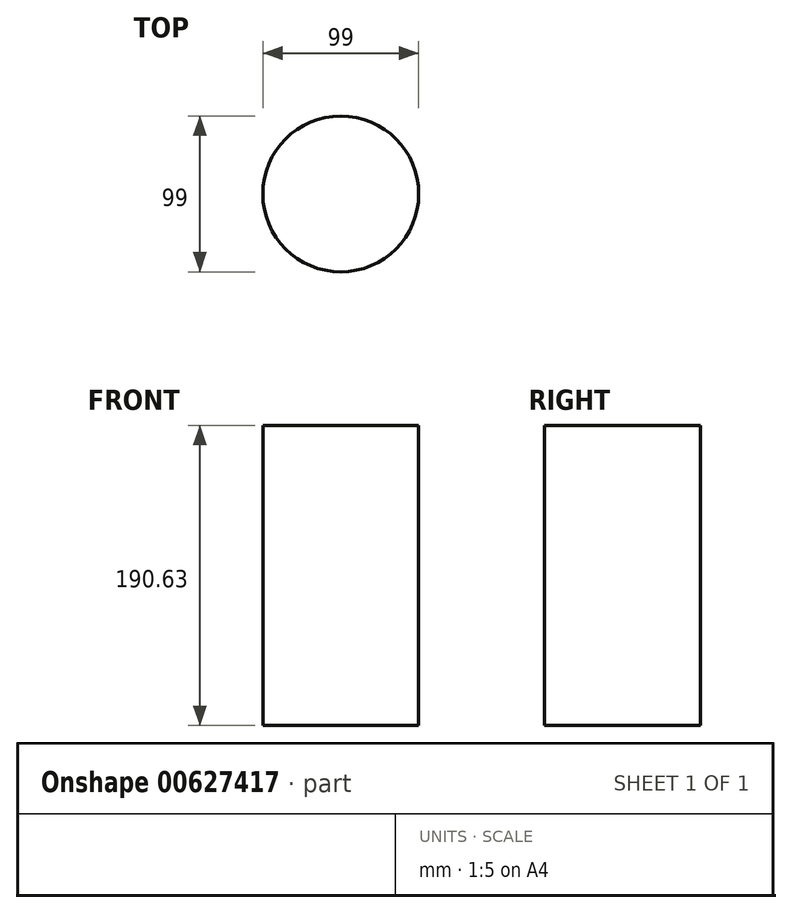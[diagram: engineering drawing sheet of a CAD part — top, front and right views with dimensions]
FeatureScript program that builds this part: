
annotation { "Feature Type Name" : "Feature", "Feature Type Description" : "" }
export const myFeature = defineFeature(function(context is Context, id is Id, definition is map)
    precondition{}
    {
        {
            var Q0;
            Q0=qCreatedBy(makeId("Top.planeOp"),FACE);
            var sketch = newSketch(context, id + "F0", { "sketchPlane" : qUnion([Q0])});
            skCircle(sketch, "E0", {"center": v(0, 0) * mm, "radius": 49.5 * mm});
            skSolve(sketch);
        }
        {
            var Q0;
            Q0=sQuery(id+"F0.wireOp",EDGE,"E0");
            extrude(context, id + "F1", {"bodyType" : ToolBodyType.SURFACE, "surfaceEntities" : qUnion([Q0]), "depth" : 190.63 * mm, "offsetDistance" : 25.4 * mm});
        }
    });
